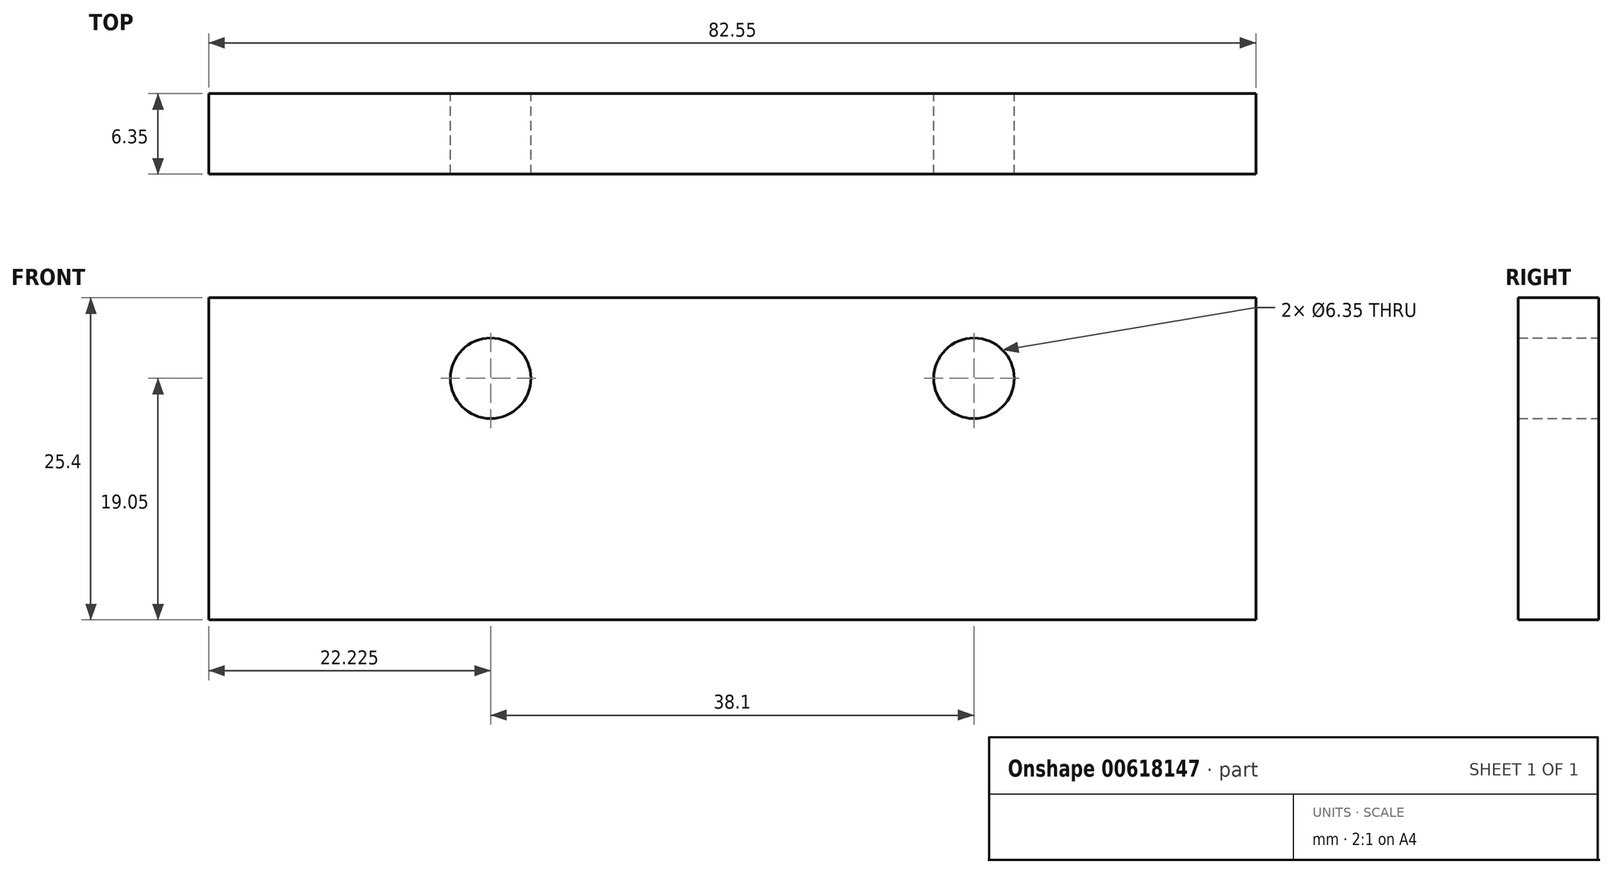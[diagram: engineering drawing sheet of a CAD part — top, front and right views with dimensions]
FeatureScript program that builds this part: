
annotation { "Feature Type Name" : "Feature", "Feature Type Description" : "" }
export const myFeature = defineFeature(function(context is Context, id is Id, definition is map)
    precondition{}
    {
        {
            var Q0;
            Q0=qCreatedBy(makeId("Front.planeOp"),FACE);
            var sketch = newSketch(context, id + "F0", { "sketchPlane" : qUnion([Q0])});
            skLineSegment(sketch, "E0.bottom", {"start": v(0, 0) * mm, "end": v(82.55, 0) * mm});
            skLineSegment(sketch, "E0.top", {"start": v(0, 25.4) * mm, "end": v(82.55, 25.4) * mm});
            skLineSegment(sketch, "E0.left", {"start": v(0, 0) * mm, "end": v(0, 25.4) * mm});
            skLineSegment(sketch, "E0.right", {"start": v(82.55, 0) * mm, "end": v(82.55, 25.4) * mm});
            skCircle(sketch, "E1", {"center": v(22.22, 19.05) * mm, "radius": 3.18 * mm});
            skCircle(sketch, "E2", {"center": v(60.33, 19.05) * mm, "radius": 3.18 * mm});
            skSolve(sketch);
        }
        {
            var Q0;
            Q0=qSketchRegion(id+"F0",true);
            extrude(context, id + "F1", {"entities" : qUnion([Q0]), "depth" : 6.35 * mm});
        }
    });
